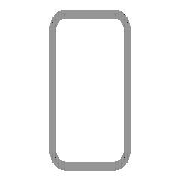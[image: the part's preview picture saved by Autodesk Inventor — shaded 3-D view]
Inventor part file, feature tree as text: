
AUTODESK INVENTOR PART (.ipt)
format: ipt  version: 2025 (Build 290162010, 162A)  size: 135,680 bytes
history: native  units: mm (DEFAULTED — no unit token found)
features: other x4, sketch x1, plane x1
ambient origin geometry x8: Origin, YZ Plane, XZ Plane, XY Plane, X Axis, Y Axis, Z Axis, Center Point
bodies: Solid1 (feature_tree), Body (feature_tree)
feature tree (6):
  parser-record x1  (decoder bookkeeping rows leaked as tree rows — omitted from the tree; the rows remain in map.json)
  other  "Driven Length"
  other  "Start Plane"
  other  "End Plane"
  sketch  "Sketch3"  dims[d3=1000.0mm d4=0.0mm d7=4.0mm d9=20.0mm d11=40.0mm d12=2.0mm d13=-0.0mm d14=1000.0mm d15=10.0mm d16=20.0mm d17=90.0deg d18=1000.0mm]
  plane  "Work Plane3"
